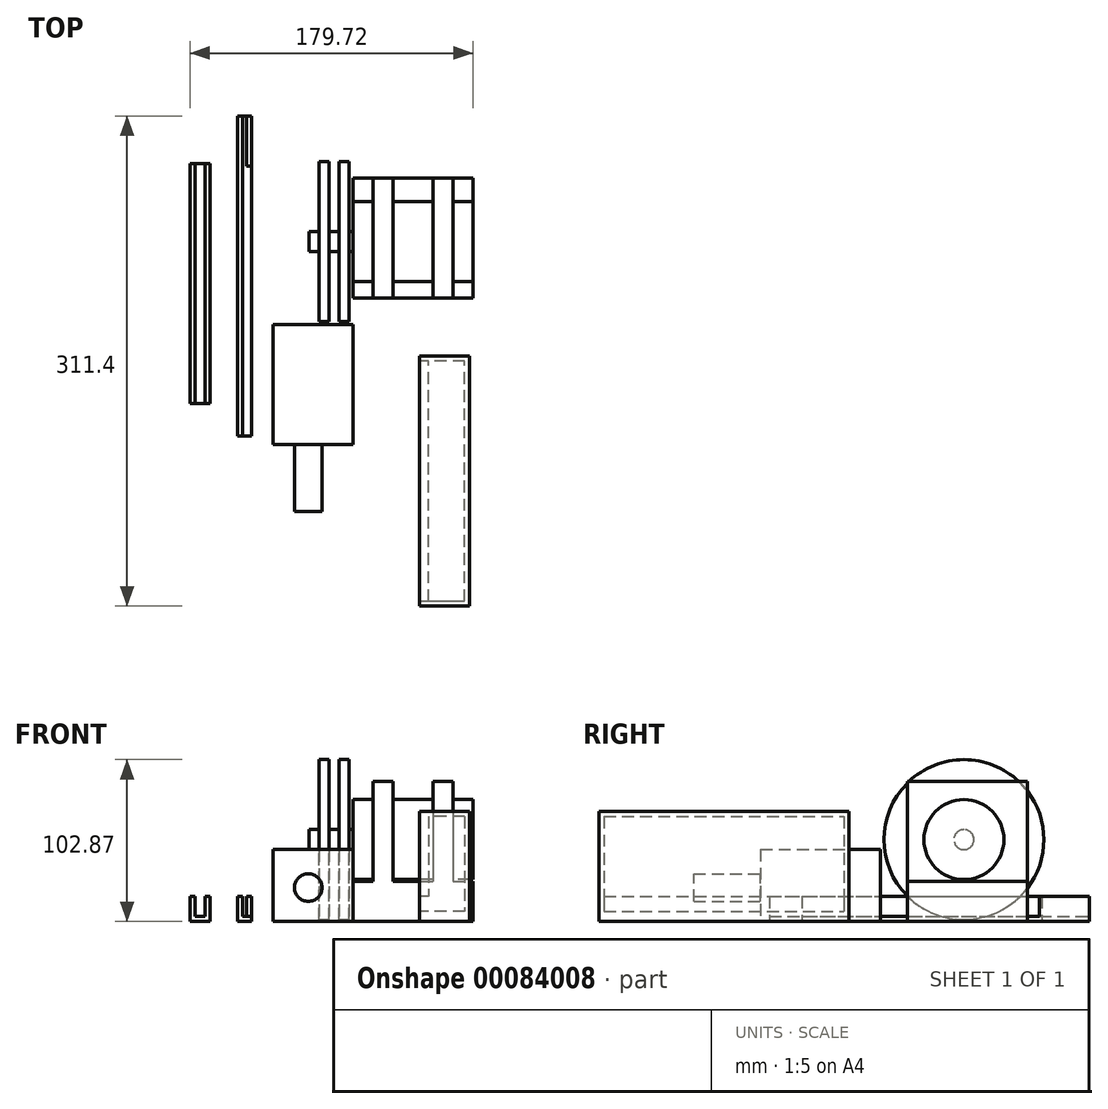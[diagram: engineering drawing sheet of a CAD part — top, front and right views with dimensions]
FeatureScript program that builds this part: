
annotation { "Feature Type Name" : "Feature", "Feature Type Description" : "" }
export const myFeature = defineFeature(function(context is Context, id is Id, definition is map)
    precondition{}
    {
        {
            var Q0;
            Q0=qCreatedBy(makeId("Top.planeOp"),FACE);
            var sketch = newSketch(context, id + "F0", { "sketchPlane" : qUnion([Q0])});
            skLineSegment(sketch, "E0.bottom", {"start": v(0, 0) * mm, "end": v(76.2, 0) * mm});
            skLineSegment(sketch, "E0.top", {"start": v(0, 76.2) * mm, "end": v(76.2, 76.2) * mm});
            skLineSegment(sketch, "E0.left", {"start": v(0, 0) * mm, "end": v(0, 76.2) * mm});
            skLineSegment(sketch, "E0.right", {"start": v(76.2, 0) * mm, "end": v(76.2, 76.2) * mm});
            skSolve(sketch);
        }
        {
            var Q0;
            Q0=makeQuery(id+"F0.imprint","IMPRINT",FACE,{"disambiguationData":[TD([[makeQuery(id+"F0.imprint","IMPRINT",EDGE,{"derivedFrom":sQuery(id+"F0.wireOp",EDGE,"E0.bottom")}),1.0]])]});
            extrude(context, id + "F1", {"entities" : qUnion([Q0]), "depth" : 25.4 * mm});
        }
        {
            var Q0;
            Q0=makeQuery(id+"F1.opExtrude","CAP_FACE",FACE,{"disambiguationData":[OSD([sQuery(id+"F0.wireOp",EDGE,"E0.bottom"),sQuery(id+"F0.wireOp",EDGE,"E0.top"),sQuery(id+"F0.wireOp",EDGE,"E0.left"),sQuery(id+"F0.wireOp",EDGE,"E0.right")])],"isStart":false});
            var sketch = newSketch(context, id + "F2", { "sketchPlane" : qUnion([Q0])});
            skLineSegment(sketch, "E1.bottom", {"start": v(63.5, 0) * mm, "end": v(50.8, 0) * mm});
            skLineSegment(sketch, "E1.top", {"start": v(63.5, 76.2) * mm, "end": v(50.8, 76.2) * mm});
            skLineSegment(sketch, "E1.left", {"start": v(63.5, 0) * mm, "end": v(63.5, 76.2) * mm});
            skLineSegment(sketch, "E1.right", {"start": v(50.8, 0) * mm, "end": v(50.8, 76.2) * mm});
            skLineSegment(sketch, "E2.bottom", {"start": v(12.7, 0) * mm, "end": v(25.4, 0) * mm});
            skLineSegment(sketch, "E2.top", {"start": v(12.7, 76.2) * mm, "end": v(25.4, 76.2) * mm});
            skLineSegment(sketch, "E2.left", {"start": v(12.7, 0) * mm, "end": v(12.7, 76.2) * mm});
            skLineSegment(sketch, "E2.right", {"start": v(25.4, 0) * mm, "end": v(25.4, 76.2) * mm});
            skSolve(sketch);
        }
        {
            var Q0;
            Q0=makeQuery(id+"F2.imprint","IMPRINT",FACE,{"disambiguationData":[TD([[makeQuery(id+"F2.imprint","IMPRINT",EDGE,{"derivedFrom":sQuery(id+"F2.wireOp",EDGE,"E1.bottom")}),1.0]])]});
            var Q1;
            Q1=makeQuery(id+"F2.imprint","IMPRINT",FACE,{"disambiguationData":[TD([[makeQuery(id+"F2.imprint","IMPRINT",EDGE,{"derivedFrom":sQuery(id+"F2.wireOp",EDGE,"E2.bottom")}),1.0]])]});
            extrude(context, id + "F3", {"entities" : qUnion([Q0, Q1]), "operationType" : NewBodyOperationType.ADD, "depth" : 63.5 * mm});
        }
        {
            var Q0;
            Q0=makeQuery(id+"F3.opExtrude","SWEPT_FACE",FACE,{"disambiguationData":[OSD([sQuery(id+"F2.wireOp",EDGE,"E1.left")])]});
            var sketch = newSketch(context, id + "F4", { "sketchPlane" : qUnion([Q0])});
            skCircle(sketch, "E3", {"center": v(36.02, 52.07) * mm, "radius": 25.4 * mm});
            skSolve(sketch);
        }
        {
            var Q0;
            Q0=makeQuery(id+"F4.imprint","IMPRINT",FACE,{"disambiguationData":[TD([[makeQuery(id+"F4.imprint","IMPRINT",EDGE,{"derivedFrom":sQuery(id+"F4.wireOp",EDGE,"E3")}),1.0]])]});
            extrude(context, id + "F5", {"entities" : qUnion([Q0]), "operationType" : NewBodyOperationType.ADD, "depth" : 12.7 * mm, "hasSecondDirection" : true, "secondDirectionOppositeDirection" : true, "secondDirectionDepth" : 63.5 * mm});
        }
        {
            var Q0;
            Q0=makeQuery(id+"F5.opExtrude","CAP_FACE",FACE,{"disambiguationData":[OSD([sQuery(id+"F4.wireOp",EDGE,"E3")])],"isStart":true});
            var sketch = newSketch(context, id + "F6", { "sketchPlane" : qUnion([Q0])});
            skCircle(sketch, "E4", {"center": v(-36.02, 52.07) * mm, "radius": 3.18 * mm});
            skSolve(sketch);
        }
        {
            var Q0;
            Q0=makeQuery(id+"F6.imprint","IMPRINT",FACE,{"disambiguationData":[TD([[makeQuery(id+"F6.imprint","IMPRINT",EDGE,{"derivedFrom":sQuery(id+"F6.wireOp",EDGE,"E4")}),1.0]])]});
            extrude(context, id + "F7", {"entities" : qUnion([Q0]), "operationType" : NewBodyOperationType.ADD, "depth" : 2.54 * mm});
        }
        {
            var Q0;
            Q0=makeQuery(id+"F7.opExtrude","CAP_FACE",FACE,{"disambiguationData":[OSD([sQuery(id+"F6.wireOp",EDGE,"E4")])],"isStart":false});
            var sketch = newSketch(context, id + "F8", { "sketchPlane" : qUnion([Q0])});
            skCircle(sketch, "E5", {"center": v(-36.02, 52.07) * mm, "radius": 50.8 * mm});
            skSolve(sketch);
        }
        {
            var Q0;
            Q0=makeQuery(id+"F8.imprint","IMPRINT",FACE,{"disambiguationData":[TD([[makeQuery(id+"F8.imprint","IMPRINT",EDGE,{"derivedFrom":makeQuery(id+"F7.opExtrude","CAP_EDGE",EDGE,{"disambiguationData":[OSD([sQuery(id+"F6.wireOp",EDGE,"E4")])],"isStart":false})}),1.0]])]});
            var Q1;
            Q1=makeQuery(id+"F8.imprint","IMPRINT",FACE,{"disambiguationData":[TD([[makeQuery(id+"F8.imprint","IMPRINT",EDGE,{"derivedFrom":sQuery(id+"F8.wireOp",EDGE,"E5")}),1.0]])]});
            extrude(context, id + "F9", {"entities" : qUnion([Q0, Q1]), "operationType" : NewBodyOperationType.ADD, "depth" : 6.35 * mm});
        }
        {
            var Q0;
            Q0=makeQuery(id+"F9.opExtrude","CAP_FACE",FACE,{"disambiguationData":[OSD([sQuery(id+"F8.wireOp",EDGE,"E5")])],"isStart":false});
            var sketch = newSketch(context, id + "F10", { "sketchPlane" : qUnion([Q0])});
            skCircle(sketch, "E6", {"center": v(-36.02, 52.07) * mm, "radius": 6.35 * mm});
            skSolve(sketch);
        }
        {
            var Q0;
            Q0=makeQuery(id+"F10.imprint","IMPRINT",FACE,{"disambiguationData":[TD([[makeQuery(id+"F10.imprint","IMPRINT",EDGE,{"derivedFrom":sQuery(id+"F10.wireOp",EDGE,"E6")}),1.0]])]});
            extrude(context, id + "F11", {"entities" : qUnion([Q0]), "operationType" : NewBodyOperationType.ADD, "depth" : 6.35 * mm, "hasSecondDirection" : true, "secondDirectionOppositeDirection" : true, "secondDirectionDepth" : 25.4 * mm});
        }
        {
            var Q0;
            Q0=makeQuery(id+"F11.opExtrude","CAP_FACE",FACE,{"disambiguationData":[OSD([sQuery(id+"F10.wireOp",EDGE,"E6")])],"isStart":false});
            var sketch = newSketch(context, id + "F12", { "sketchPlane" : qUnion([Q0])});
            skCircle(sketch, "E7", {"center": v(-36.02, 52.07) * mm, "radius": 50.8 * mm});
            skSolve(sketch);
        }
        {
            var Q0;
            Q0=makeQuery(id+"F12.imprint","IMPRINT",FACE,{"disambiguationData":[TD([[makeQuery(id+"F12.imprint","IMPRINT",EDGE,{"derivedFrom":makeQuery(id+"F11.opExtrude","CAP_EDGE",EDGE,{"disambiguationData":[OSD([sQuery(id+"F10.wireOp",EDGE,"E6")])],"isStart":false})}),1.0]])]});
            var Q1;
            Q1=makeQuery(id+"F12.imprint","IMPRINT",FACE,{"disambiguationData":[TD([[makeQuery(id+"F12.imprint","IMPRINT",EDGE,{"derivedFrom":sQuery(id+"F12.wireOp",EDGE,"E7")}),1.0]])]});
            extrude(context, id + "F13", {"entities" : qUnion([Q0, Q1]), "operationType" : NewBodyOperationType.ADD, "depth" : 6.35 * mm});
        }
        {
            var Q0;
            Q0=makeQuery(id+"F13.opExtrude","CAP_FACE",FACE,{"disambiguationData":[OSD([sQuery(id+"F12.wireOp",EDGE,"E7")])],"isStart":false});
            var sketch = newSketch(context, id + "F14", { "sketchPlane" : qUnion([Q0])});
            skCircle(sketch, "E8", {"center": v(-36.02, 52.07) * mm, "radius": 6.35 * mm});
            skSolve(sketch);
        }
        {
            var Q0;
            Q0=makeQuery(id+"F14.imprint","IMPRINT",FACE,{"disambiguationData":[TD([[makeQuery(id+"F14.imprint","IMPRINT",EDGE,{"derivedFrom":sQuery(id+"F14.wireOp",EDGE,"E8")}),1.0]])]});
            extrude(context, id + "F15", {"entities" : qUnion([Q0]), "operationType" : NewBodyOperationType.ADD, "depth" : 6.35 * mm, "hasSecondDirection" : true, "secondDirectionOppositeDirection" : true, "secondDirectionDepth" : 25.4 * mm});
        }
        {
            var Q0;
            Q0=qCreatedBy(makeId("Top.planeOp"),FACE);
            var sketch = newSketch(context, id + "F16", { "sketchPlane" : qUnion([Q0])});
            skLineSegment(sketch, "E9.bottom", {"start": v(-73.4, -87.52) * mm, "end": v(-64.5, -87.52) * mm});
            skLineSegment(sketch, "E9.top", {"start": v(-73.4, 115.68) * mm, "end": v(-64.5, 115.68) * mm});
            skLineSegment(sketch, "E9.left", {"start": v(-73.4, -87.52) * mm, "end": v(-73.4, 115.68) * mm});
            skLineSegment(sketch, "E9.right", {"start": v(-64.5, -87.52) * mm, "end": v(-64.5, 115.68) * mm});
            skSolve(sketch);
        }
        {
            var Q0;
            Q0=makeQuery(id+"F16.imprint","IMPRINT",FACE,{"disambiguationData":[TD([[makeQuery(id+"F16.imprint","IMPRINT",EDGE,{"derivedFrom":sQuery(id+"F16.wireOp",EDGE,"E9.bottom")}),1.0]])]});
            extrude(context, id + "F17", {"entities" : qUnion([Q0]), "depth" : 3.17 * mm});
        }
        {
            var Q0;
            Q0=makeQuery(id+"F17.opExtrude","CAP_FACE",FACE,{"disambiguationData":[OSD([sQuery(id+"F16.wireOp",EDGE,"E9.bottom"),sQuery(id+"F16.wireOp",EDGE,"E9.top"),sQuery(id+"F16.wireOp",EDGE,"E9.left"),sQuery(id+"F16.wireOp",EDGE,"E9.right")])],"isStart":false});
            var sketch = newSketch(context, id + "F18", { "sketchPlane" : qUnion([Q0])});
            skLineSegment(sketch, "E10.bottom", {"start": v(-73.4, -87.52) * mm, "end": v(-70.22, -87.52) * mm});
            skLineSegment(sketch, "E10.top", {"start": v(-73.4, 115.68) * mm, "end": v(-70.22, 115.68) * mm});
            skLineSegment(sketch, "E10.left", {"start": v(-73.4, -87.52) * mm, "end": v(-73.4, 115.68) * mm});
            skLineSegment(sketch, "E10.right", {"start": v(-70.22, -87.52) * mm, "end": v(-70.22, 115.68) * mm});
            skLineSegment(sketch, "E11.bottom", {"start": v(-64.5, -87.52) * mm, "end": v(-67.68, -87.52) * mm});
            skLineSegment(sketch, "E11.top", {"start": v(-64.5, 115.68) * mm, "end": v(-67.68, 115.68) * mm});
            skLineSegment(sketch, "E11.left", {"start": v(-64.5, -87.52) * mm, "end": v(-64.5, 115.68) * mm});
            skLineSegment(sketch, "E11.right", {"start": v(-67.68, -87.52) * mm, "end": v(-67.68, 115.68) * mm});
            skSolve(sketch);
        }
        {
            var Q0;
            Q0=makeQuery(id+"F18.imprint","IMPRINT",FACE,{"disambiguationData":[TD([[makeQuery(id+"F18.imprint","IMPRINT",EDGE,{"derivedFrom":sQuery(id+"F18.wireOp",EDGE,"E10.bottom")}),1.0]])]});
            var Q1;
            Q1=makeQuery(id+"F18.imprint","IMPRINT",FACE,{"disambiguationData":[TD([[makeQuery(id+"F18.imprint","IMPRINT",EDGE,{"derivedFrom":sQuery(id+"F18.wireOp",EDGE,"E11.bottom")}),1.0]])]});
            extrude(context, id + "F19", {"entities" : qUnion([Q0, Q1]), "operationType" : NewBodyOperationType.ADD, "depth" : 12.7 * mm});
        }
        {
            var Q0;
            Q0=qCreatedBy(makeId("Top.planeOp"),FACE);
            var sketch = newSketch(context, id + "F20", { "sketchPlane" : qUnion([Q0])});
            skLineSegment(sketch, "E12.bottom", {"start": v(-50.8, -93.05) * mm, "end": v(0, -93.05) * mm});
            skLineSegment(sketch, "E12.top", {"start": v(-50.8, -16.85) * mm, "end": v(0, -16.85) * mm});
            skLineSegment(sketch, "E12.left", {"start": v(-50.8, -93.05) * mm, "end": v(-50.8, -16.85) * mm});
            skLineSegment(sketch, "E12.right", {"start": v(0, -93.05) * mm, "end": v(0, -16.85) * mm});
            skSolve(sketch);
        }
        {
            var Q0;
            Q0=makeQuery(id+"F20.imprint","IMPRINT",FACE,{"disambiguationData":[TD([[makeQuery(id+"F20.imprint","IMPRINT",EDGE,{"derivedFrom":sQuery(id+"F20.wireOp",EDGE,"E12.bottom")}),1.0]])]});
            extrude(context, id + "F21", {"entities" : qUnion([Q0]), "depth" : 45.72 * mm});
        }
        {
            var Q0;
            Q0=makeQuery(id+"F21.opExtrude","SWEPT_FACE",FACE,{"disambiguationData":[OSD([sQuery(id+"F20.wireOp",EDGE,"E12.bottom")])]});
            var sketch = newSketch(context, id + "F22", { "sketchPlane" : qUnion([Q0])});
            skCircle(sketch, "E13", {"center": v(-28.48, 21.6) * mm, "radius": 8.76 * mm});
            skSolve(sketch);
        }
        {
            var Q0;
            Q0=makeQuery(id+"F22.imprint","IMPRINT",FACE,{"disambiguationData":[TD([[makeQuery(id+"F22.imprint","IMPRINT",EDGE,{"derivedFrom":sQuery(id+"F22.wireOp",EDGE,"E13")}),1.0]])]});
            extrude(context, id + "F23", {"entities" : qUnion([Q0]), "operationType" : NewBodyOperationType.ADD, "depth" : 42.42 * mm});
        }
        {
            var Q0;
            Q0=qCreatedBy(makeId("Top.planeOp"),FACE);
            var sketch = newSketch(context, id + "F24", { "sketchPlane" : qUnion([Q0])});
            skLineSegment(sketch, "E14.bottom", {"start": v(42.25, -195.72) * mm, "end": v(74, -195.72) * mm});
            skLineSegment(sketch, "E14.top", {"start": v(42.25, -36.97) * mm, "end": v(74, -36.97) * mm});
            skLineSegment(sketch, "E14.left", {"start": v(42.25, -195.72) * mm, "end": v(42.25, -36.97) * mm});
            skLineSegment(sketch, "E14.right", {"start": v(74, -195.72) * mm, "end": v(74, -36.97) * mm});
            skSolve(sketch);
        }
        {
            var Q0;
            Q0=makeQuery(id+"F24.imprint","IMPRINT",FACE,{"disambiguationData":[TD([[makeQuery(id+"F24.imprint","IMPRINT",EDGE,{"derivedFrom":sQuery(id+"F24.wireOp",EDGE,"E14.bottom")}),1.0]])]});
            extrude(context, id + "F25", {"entities" : qUnion([Q0]), "operationType" : NewBodyOperationType.ADD, "depth" : 6.35 * mm});
        }
        {
            var Q0;
            Q0=makeQuery(id+"F25.opExtrude","CAP_FACE",FACE,{"disambiguationData":[OSD([sQuery(id+"F24.wireOp",EDGE,"E14.bottom"),sQuery(id+"F24.wireOp",EDGE,"E14.top"),sQuery(id+"F24.wireOp",EDGE,"E14.left"),sQuery(id+"F24.wireOp",EDGE,"E14.right")])],"isStart":false});
            var sketch = newSketch(context, id + "F26", { "sketchPlane" : qUnion([Q0])});
            skLineSegment(sketch, "E15.0", {"start": v(45.42, -192.54) * mm, "end": v(45.42, -40.14) * mm});
            skLineSegment(sketch, "E15.1", {"start": v(45.42, -192.54) * mm, "end": v(70.82, -192.54) * mm});
            skLineSegment(sketch, "E15.2", {"start": v(70.82, -192.54) * mm, "end": v(70.82, -40.14) * mm});
            skLineSegment(sketch, "E15.3", {"start": v(45.42, -40.14) * mm, "end": v(70.82, -40.14) * mm});
            skLineSegment(sketch, "E16", {"start": v(45.42, -40.14) * mm, "end": v(42.25, -40.14) * mm});
            skLineSegment(sketch, "E17", {"start": v(45.42, -192.54) * mm, "end": v(42.25, -192.54) * mm});
            skSolve(sketch);
        }
        {
            var Q0;
            Q0=makeQuery(id+"F26.imprint","IMPRINT",FACE,{"disambiguationData":[TD([[makeQuery(id+"F26.imprint","IMPRINT",EDGE,{"derivedFrom":sQuery(id+"F26.wireOp",EDGE,"E15.1")}),-1.0]])]});
            extrude(context, id + "F27", {"entities" : qUnion([Q0]), "operationType" : NewBodyOperationType.ADD, "depth" : 9.52 * mm});
        }
        {
            var Q0;
            Q0=makeQuery(id+"F27.opExtrude","CAP_FACE",FACE,{"disambiguationData":[OSD([sQuery(id+"F24.wireOp",EDGE,"E14.bottom"),sQuery(id+"F24.wireOp",EDGE,"E14.top"),sQuery(id+"F24.wireOp",EDGE,"E14.left"),sQuery(id+"F24.wireOp",EDGE,"E14.right"),sQuery(id+"F26.wireOp",EDGE,"E15.1"),sQuery(id+"F26.wireOp",EDGE,"E15.2"),sQuery(id+"F26.wireOp",EDGE,"E15.3"),sQuery(id+"F26.wireOp",EDGE,"E16"),sQuery(id+"F26.wireOp",EDGE,"E17")])],"isStart":false});
            var sketch = newSketch(context, id + "F28", { "sketchPlane" : qUnion([Q0])});
            skLineSegment(sketch, "E18.bottom", {"start": v(42.25, -195.72) * mm, "end": v(74, -195.72) * mm});
            skLineSegment(sketch, "E18.top", {"start": v(42.25, -36.97) * mm, "end": v(74, -36.97) * mm});
            skLineSegment(sketch, "E18.left", {"start": v(42.25, -195.72) * mm, "end": v(42.25, -36.97) * mm});
            skLineSegment(sketch, "E18.right", {"start": v(74, -195.72) * mm, "end": v(74, -36.97) * mm});
            skLineSegment(sketch, "E19", {"start": v(48, -192.54) * mm, "end": v(48, -40.14) * mm});
            skSolve(sketch);
        }
        {
            var Q0;
            {var subQ5=sQuery(id+"F28.wireOp",EDGE,"E19");Q0=makeQuery(id+"F28.imprint","IMPRINT",FACE,{"disambiguationData":[TD([[makeQuery(id+"F28.imprint","IMPRINT",EDGE,{"derivedFrom":subQ5}),1.0]])]});}
            var Q1;
            {var subQ4=sQuery(id+"F28.wireOp",EDGE,"E18.bottom");Q1=makeQuery(id+"F28.imprint","IMPRINT",FACE,{"disambiguationData":[TD([[makeQuery(id+"F28.imprint","IMPRINT",EDGE,{"derivedFrom":subQ4}),1.0]])]});}
            extrude(context, id + "F29", {"entities" : qUnion([Q0, Q1]), "operationType" : NewBodyOperationType.ADD, "depth" : 50.8 * mm});
        }
        {
            var Q0;
            Q0=makeQuery(id+"F29.opExtrude","CAP_FACE",FACE,{"disambiguationData":[OSD([sQuery(id+"F26.wireOp",EDGE,"E15.1"),sQuery(id+"F26.wireOp",EDGE,"E15.2"),sQuery(id+"F26.wireOp",EDGE,"E15.3"),sQuery(id+"F26.wireOp",EDGE,"E16"),sQuery(id+"F26.wireOp",EDGE,"E17"),sQuery(id+"F28.wireOp",EDGE,"E18.bottom"),sQuery(id+"F28.wireOp",EDGE,"E18.top"),sQuery(id+"F28.wireOp",EDGE,"E18.left"),sQuery(id+"F28.wireOp",EDGE,"E18.right"),sQuery(id+"F28.wireOp",EDGE,"E19")])],"isStart":false});
            var sketch = newSketch(context, id + "F30", { "sketchPlane" : qUnion([Q0])});
            skLineSegment(sketch, "E20.bottom", {"start": v(42.25, -195.72) * mm, "end": v(74, -195.72) * mm});
            skLineSegment(sketch, "E20.top", {"start": v(42.25, -36.97) * mm, "end": v(74, -36.97) * mm});
            skLineSegment(sketch, "E20.left", {"start": v(42.25, -195.72) * mm, "end": v(42.25, -36.97) * mm});
            skLineSegment(sketch, "E20.right", {"start": v(74, -195.72) * mm, "end": v(74, -36.97) * mm});
            skSolve(sketch);
        }
        {
            var Q0;
            Q0=makeQuery(id+"F30.imprint","IMPRINT",FACE,{"disambiguationData":[TD([[makeQuery(id+"F30.imprint","IMPRINT",EDGE,{"derivedFrom":makeQuery(id+"F29.opExtrude","CAP_EDGE",EDGE,{"disambiguationData":[OSD([sQuery(id+"F28.wireOp",EDGE,"E19")])],"isStart":false})}),-1.0]])]});
            var Q1;
            Q1=makeQuery(id+"F30.imprint","IMPRINT",FACE,{"disambiguationData":[TD([[makeQuery(id+"F30.imprint","IMPRINT",EDGE,{"derivedFrom":sQuery(id+"F30.wireOp",EDGE,"E20.bottom")}),1.0]])]});
            extrude(context, id + "F31", {"entities" : qUnion([Q0, Q1]), "operationType" : NewBodyOperationType.ADD, "depth" : 3.17 * mm});
        }
        {
            var Q0;
            Q0=makeQuery(id+"F19.opExtrude","CAP_FACE",FACE,{"disambiguationData":[OSD([sQuery(id+"F18.wireOp",EDGE,"E11.bottom"),sQuery(id+"F18.wireOp",EDGE,"E11.top"),sQuery(id+"F18.wireOp",EDGE,"E11.left"),sQuery(id+"F18.wireOp",EDGE,"E11.right")])],"isStart":false});
            var sketch = newSketch(context, id + "F32", { "sketchPlane" : qUnion([Q0])});
            skLineSegment(sketch, "E21", {"start": v(-67.68, 83.93) * mm, "end": v(-64.5, 83.93) * mm});
            skSolve(sketch);
        }
        {
            var Q0;
            {var subQ0=sQuery(id+"F32.wireOp",EDGE,"E21");Q0=makeQuery(id+"F32.imprint","IMPRINT",FACE,{"disambiguationData":[TD([[makeQuery(id+"F32.imprint","IMPRINT",EDGE,{"derivedFrom":subQ0}),-1.0]])]});}
            extrude(context, id + "F33", {"entities" : qUnion([Q0]), "operationType" : NewBodyOperationType.REMOVE, "oppositeDirection" : true, "depth" : 12.7 * mm});
        }
        {
            var Q0;
            Q0=qCreatedBy(makeId("Top.planeOp"),FACE);
            var sketch = newSketch(context, id + "F34", { "sketchPlane" : qUnion([Q0])});
            skLineSegment(sketch, "E22.bottom", {"start": v(-103.52, -66.9) * mm, "end": v(-90.82, -66.9) * mm});
            skLineSegment(sketch, "E22.top", {"start": v(-103.52, 85.5) * mm, "end": v(-90.82, 85.5) * mm});
            skLineSegment(sketch, "E22.left", {"start": v(-103.52, -66.9) * mm, "end": v(-103.52, 85.5) * mm});
            skLineSegment(sketch, "E22.right", {"start": v(-90.82, -66.9) * mm, "end": v(-90.82, 85.5) * mm});
            skSolve(sketch);
        }
        {
            var Q0;
            Q0=makeQuery(id+"F34.imprint","IMPRINT",FACE,{"disambiguationData":[TD([[makeQuery(id+"F34.imprint","IMPRINT",EDGE,{"derivedFrom":sQuery(id+"F34.wireOp",EDGE,"E22.bottom")}),1.0]])]});
            extrude(context, id + "F35", {"entities" : qUnion([Q0]), "depth" : 3.17 * mm});
        }
        {
            var Q0;
            Q0=makeQuery(id+"F35.opExtrude","CAP_FACE",FACE,{"disambiguationData":[OSD([sQuery(id+"F34.wireOp",EDGE,"E22.bottom"),sQuery(id+"F34.wireOp",EDGE,"E22.top"),sQuery(id+"F34.wireOp",EDGE,"E22.left"),sQuery(id+"F34.wireOp",EDGE,"E22.right")])],"isStart":false});
            var sketch = newSketch(context, id + "F36", { "sketchPlane" : qUnion([Q0])});
            skLineSegment(sketch, "E23.bottom", {"start": v(-100.35, -66.9) * mm, "end": v(-94, -66.9) * mm});
            skLineSegment(sketch, "E23.top", {"start": v(-100.35, 85.5) * mm, "end": v(-94, 85.5) * mm});
            skLineSegment(sketch, "E23.left", {"start": v(-100.35, -66.9) * mm, "end": v(-100.35, 85.5) * mm});
            skLineSegment(sketch, "E23.right", {"start": v(-94, -66.9) * mm, "end": v(-94, 85.5) * mm});
            skSolve(sketch);
        }
        {
            var Q0;
            {var subQ0=sQuery(id+"F36.wireOp",EDGE,"E23.left");Q0=makeQuery(id+"F36.imprint","IMPRINT",FACE,{"disambiguationData":[TD([[makeQuery(id+"F36.imprint","IMPRINT",EDGE,{"derivedFrom":subQ0}),1.0]])]});}
            var Q1;
            {var subQ0=sQuery(id+"F36.wireOp",EDGE,"E23.right");Q1=makeQuery(id+"F36.imprint","IMPRINT",FACE,{"disambiguationData":[TD([[makeQuery(id+"F36.imprint","IMPRINT",EDGE,{"derivedFrom":subQ0}),-1.0]])]});}
            extrude(context, id + "F37", {"entities" : qUnion([Q0, Q1]), "operationType" : NewBodyOperationType.ADD, "depth" : 12.7 * mm});
        }
    });
